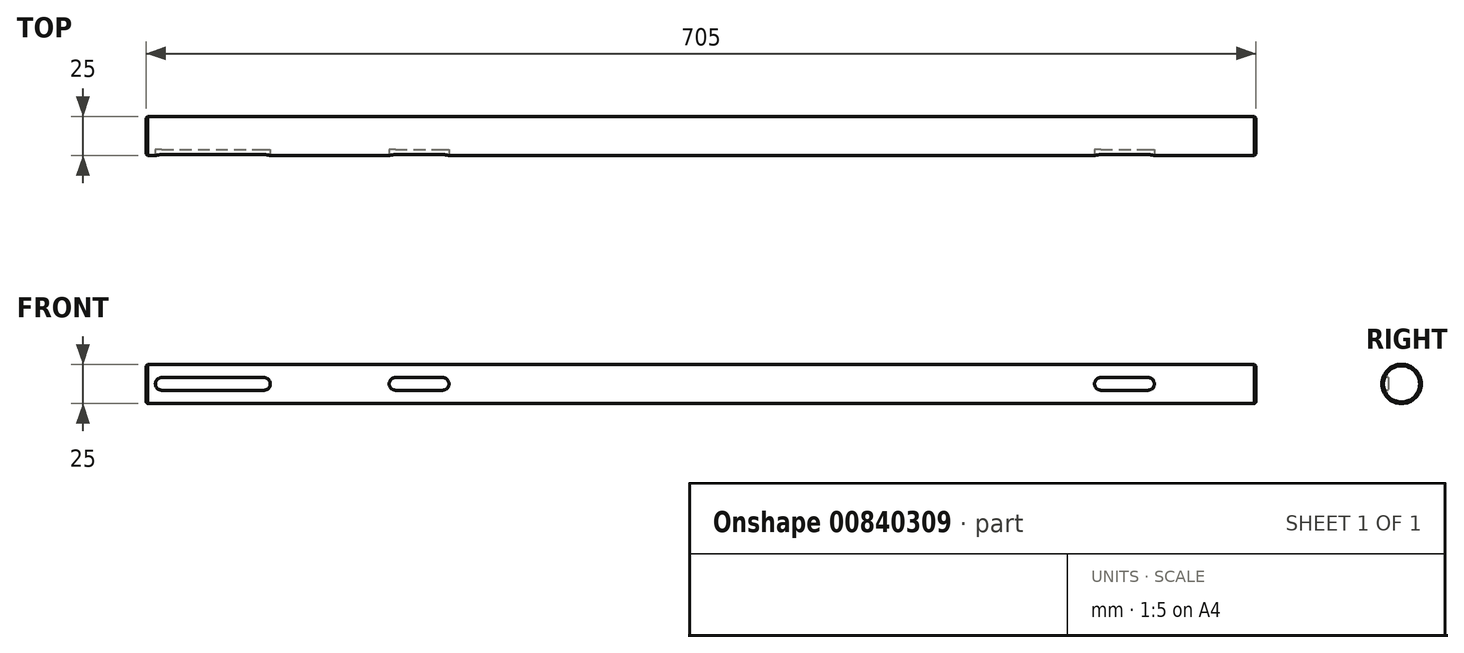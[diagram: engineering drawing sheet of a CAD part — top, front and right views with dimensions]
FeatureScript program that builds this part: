
annotation { "Feature Type Name" : "Feature", "Feature Type Description" : "" }
export const myFeature = defineFeature(function(context is Context, id is Id, definition is map)
    precondition{}
    {
        {
            var Q0;
            Q0=qCreatedBy(makeId("Right.planeOp"),FACE);
            var sketch = newSketch(context, id + "F0", { "sketchPlane" : qUnion([Q0])});
            skCircle(sketch, "E0", {"center": v(0, 0) * mm, "radius": 12.5 * mm});
            skSolve(sketch);
        }
        {
            var Q0;
            Q0 = qSketchRegion(id + "F0", true);
            extrude(context, id + "F1", {"entities" : qUnion([Q0]), "endBound" : BoundingType.SYMMETRIC, "depth" : 705 * mm, "offsetDistance" : 25 * mm});
        }
        {
            var Q0;
            Q0=qCreatedBy(makeId("Front.planeOp"),FACE);
            cPlane(context, id + "F2", {"entities" : qUnion([Q0]), "cplaneType" : CPlaneType.OFFSET, "offset" : 12.5 * mm, "width" : 150 * mm, "height" : 150 * mm});
        }
        {
            var Q0;
            Q0=qCreatedBy(id+"F2.planeOp",FACE);
            var sketch = newSketch(context, id + "F3", { "sketchPlane" : qUnion([Q0])});
            skLineSegment(sketch, "E1", {"start": v(-342.5, 0) * mm, "end": v(-277.5, 0) * mm});
            skLineSegment(sketch, "E2", {"start": v(-194, 0) * mm, "end": v(-164, 0) * mm});
            skLineSegment(sketch, "E3", {"start": v(254, 0) * mm, "end": v(284, 0) * mm});
            skArc(sketch, "E4.0.startCap", {"start": v(-342.5, -4) * mm, "mid": v(-346.5, 0) * mm, "end": v(-342.5, 4) * mm});
            skArc(sketch, "E4.0.endCap", {"start": v(-277.5, 4) * mm, "mid": v(-273.5, 0) * mm, "end": v(-277.5, -4) * mm});
            skLineSegment(sketch, "E4.0.left", {"start": v(-342.5, 4) * mm, "end": v(-277.5, 4) * mm});
            skLineSegment(sketch, "E4.0.right", {"start": v(-342.5, -4) * mm, "end": v(-277.5, -4) * mm});
            skArc(sketch, "E4.1.startCap", {"start": v(-194, -4) * mm, "mid": v(-198, 0) * mm, "end": v(-194, 4) * mm});
            skArc(sketch, "E4.1.endCap", {"start": v(-164, 4) * mm, "mid": v(-160, 0) * mm, "end": v(-164, -4) * mm});
            skLineSegment(sketch, "E4.1.left", {"start": v(-194, 4) * mm, "end": v(-164, 4) * mm});
            skLineSegment(sketch, "E4.1.right", {"start": v(-194, -4) * mm, "end": v(-164, -4) * mm});
            skArc(sketch, "E4.2.startCap", {"start": v(254, -4) * mm, "mid": v(250, 0) * mm, "end": v(254, 4) * mm});
            skArc(sketch, "E4.2.endCap", {"start": v(284, 4) * mm, "mid": v(288, 0) * mm, "end": v(284, -4) * mm});
            skLineSegment(sketch, "E4.2.left", {"start": v(254, 4) * mm, "end": v(284, 4) * mm});
            skLineSegment(sketch, "E4.2.right", {"start": v(254, -4) * mm, "end": v(284, -4) * mm});
            skSolve(sketch);
        }
        {
            var Q0;
            Q0 = qSketchRegion(id + "F3", true);
            extrude(context, id + "F4", {"entities" : qUnion([Q0]), "operationType" : NewBodyOperationType.REMOVE, "oppositeDirection" : true, "depth" : 4 * mm, "offsetDistance" : 25 * mm});
        }
        {
            var Q0;
            Q0=makeQuery(id+"F1.opExtrude","CAP_FACE",FACE,{"disambiguationData":[OSD([sQuery(id+"F0.wireOp",EDGE,"E0")])],"isStart":false});
            var Q1;
            Q1=makeQuery(id+"F1.opExtrude","CAP_FACE",FACE,{"disambiguationData":[OSD([sQuery(id+"F0.wireOp",EDGE,"E0")])],"isStart":true});
            chamfer(context, id + "F5", {"entities" : qUnion([Q0, Q1]), "width" : 1 * mm, "tangentPropagation" : true});
        }
    });
